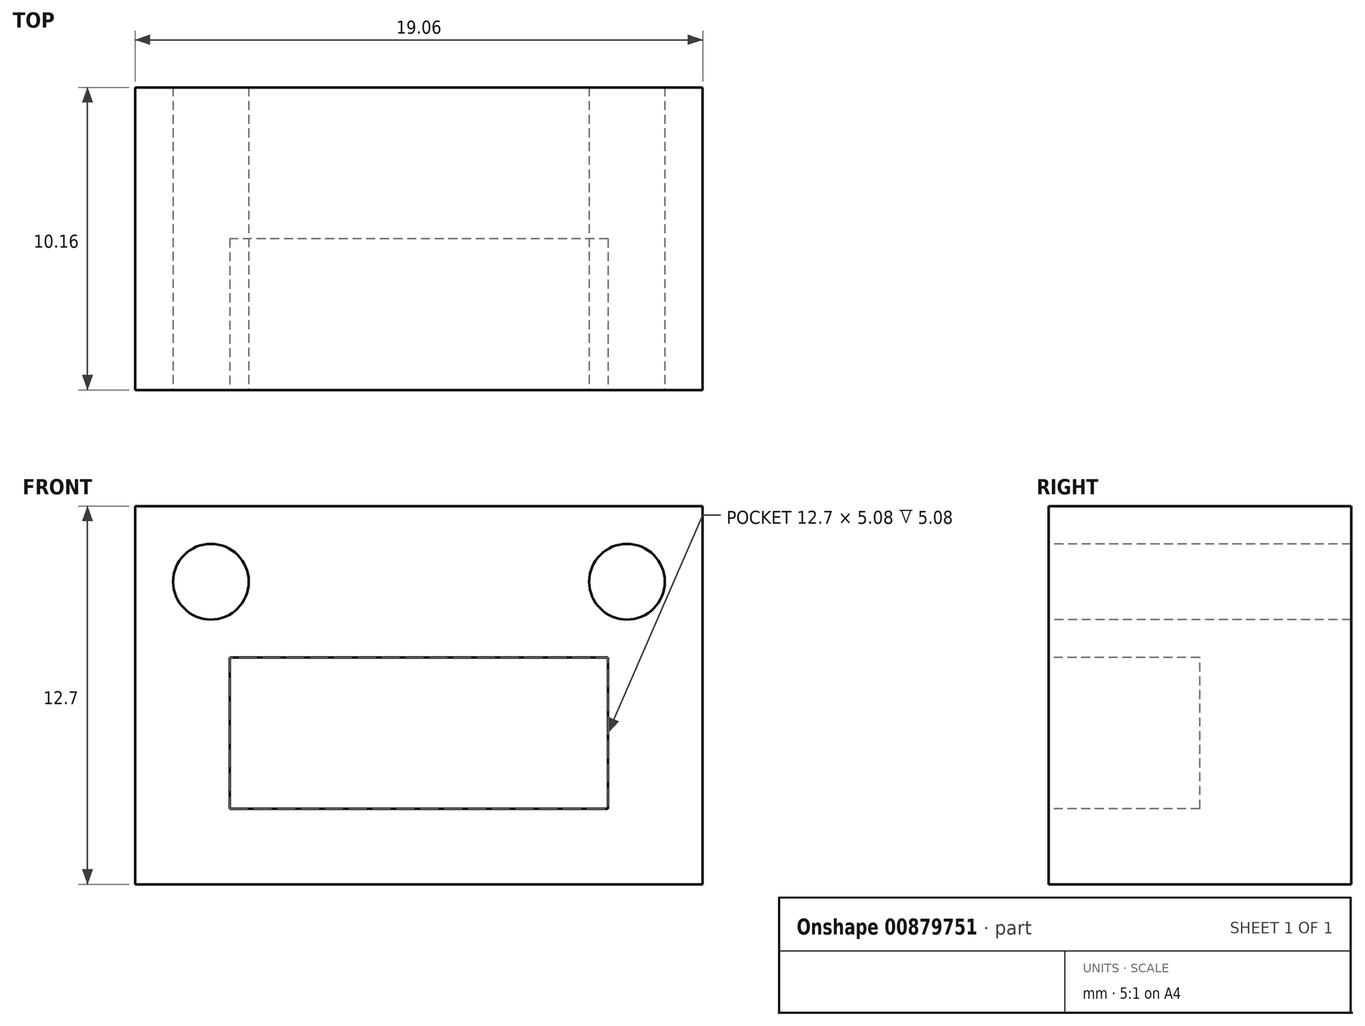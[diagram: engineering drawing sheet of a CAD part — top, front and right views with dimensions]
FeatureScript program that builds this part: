
annotation { "Feature Type Name" : "Feature", "Feature Type Description" : "" }
export const myFeature = defineFeature(function(context is Context, id is Id, definition is map)
    precondition{}
    {
        {
            var Q0;
            Q0=qCreatedBy(makeId("Front.planeOp"),FACE);
            var sketch = newSketch(context, id + "F0", { "sketchPlane" : qUnion([Q0])});
            skLineSegment(sketch, "E0.bottom", {"start": v(-9.53, 0) * mm, "end": v(9.52, 0) * mm});
            skLineSegment(sketch, "E0.top", {"start": v(-9.53, 12.7) * mm, "end": v(9.52, 12.7) * mm});
            skLineSegment(sketch, "E0.left", {"start": v(-9.53, 0) * mm, "end": v(-9.53, 12.7) * mm});
            skLineSegment(sketch, "E0.right", {"start": v(9.52, 0) * mm, "end": v(9.52, 12.7) * mm});
            skSolve(sketch);
        }
        {
            var Q0;
            Q0 = qSketchRegion(id + "F0", true);
            extrude(context, id + "F1", {"entities" : qUnion([Q0]), "depth" : 10.16 * mm, "offsetDistance" : 25.4 * mm});
        }
        {
            var Q0;
            Q0=makeQuery(id+"F1.opExtrude","CAP_FACE",FACE,{"disambiguationData":[OSD([sQuery(id+"F0.wireOp",EDGE,"E0.bottom"),sQuery(id+"F0.wireOp",EDGE,"E0.top"),sQuery(id+"F0.wireOp",EDGE,"E0.left"),sQuery(id+"F0.wireOp",EDGE,"E0.right")])],"isStart":false});
            var sketch = newSketch(context, id + "F2", { "sketchPlane" : qUnion([Q0])});
            skLineSegment(sketch, "E1.bottom", {"start": v(6.35, 2.54) * mm, "end": v(-6.35, 2.54) * mm});
            skLineSegment(sketch, "E1.top", {"start": v(6.35, 7.62) * mm, "end": v(-6.35, 7.62) * mm});
            skLineSegment(sketch, "E1.left", {"start": v(6.35, 2.54) * mm, "end": v(6.35, 7.62) * mm});
            skLineSegment(sketch, "E1.right", {"start": v(-6.35, 2.54) * mm, "end": v(-6.35, 7.62) * mm});
            skPoint(sketch, "E1.middle", {"position": v(0, 5.08) * mm});
            skPoint(sketch, "E1.middle.positionSnap0", {"position": v(0, 0) * mm});
            skPoint(sketch, "E1.centerSnap0", {"position": v(0, 0) * mm});
            skSolve(sketch);
        }
        {
            var Q0;
            Q0 = qSketchRegion(id + "F2", true);
            extrude(context, id + "F3", {"entities" : qUnion([Q0]), "operationType" : NewBodyOperationType.REMOVE, "oppositeDirection" : true, "depth" : 5.08 * mm, "offsetDistance" : 25.4 * mm});
        }
        {
            var Q0;
            Q0=makeQuery(id+"F1.opExtrude","CAP_FACE",FACE,{"disambiguationData":[OSD([sQuery(id+"F0.wireOp",EDGE,"E0.bottom"),sQuery(id+"F0.wireOp",EDGE,"E0.top"),sQuery(id+"F0.wireOp",EDGE,"E0.left"),sQuery(id+"F0.wireOp",EDGE,"E0.right")])],"isStart":false});
            var sketch = newSketch(context, id + "F4", { "sketchPlane" : qUnion([Q0])});
            skCircle(sketch, "E2", {"center": v(6.98, 10.16) * mm, "radius": 1.27 * mm});
            skCircle(sketch, "E3.MirrorC", {"center": v(-6.98, 10.16) * mm, "radius": 1.27 * mm});
            skSolve(sketch);
        }
        {
            var Q0;
            Q0 = qSketchRegion(id + "F4", true);
            extrude(context, id + "F5", {"entities" : qUnion([Q0]), "operationType" : NewBodyOperationType.REMOVE, "oppositeDirection" : true, "depth" : 10.16 * mm, "offsetDistance" : 25.4 * mm});
        }
    });
